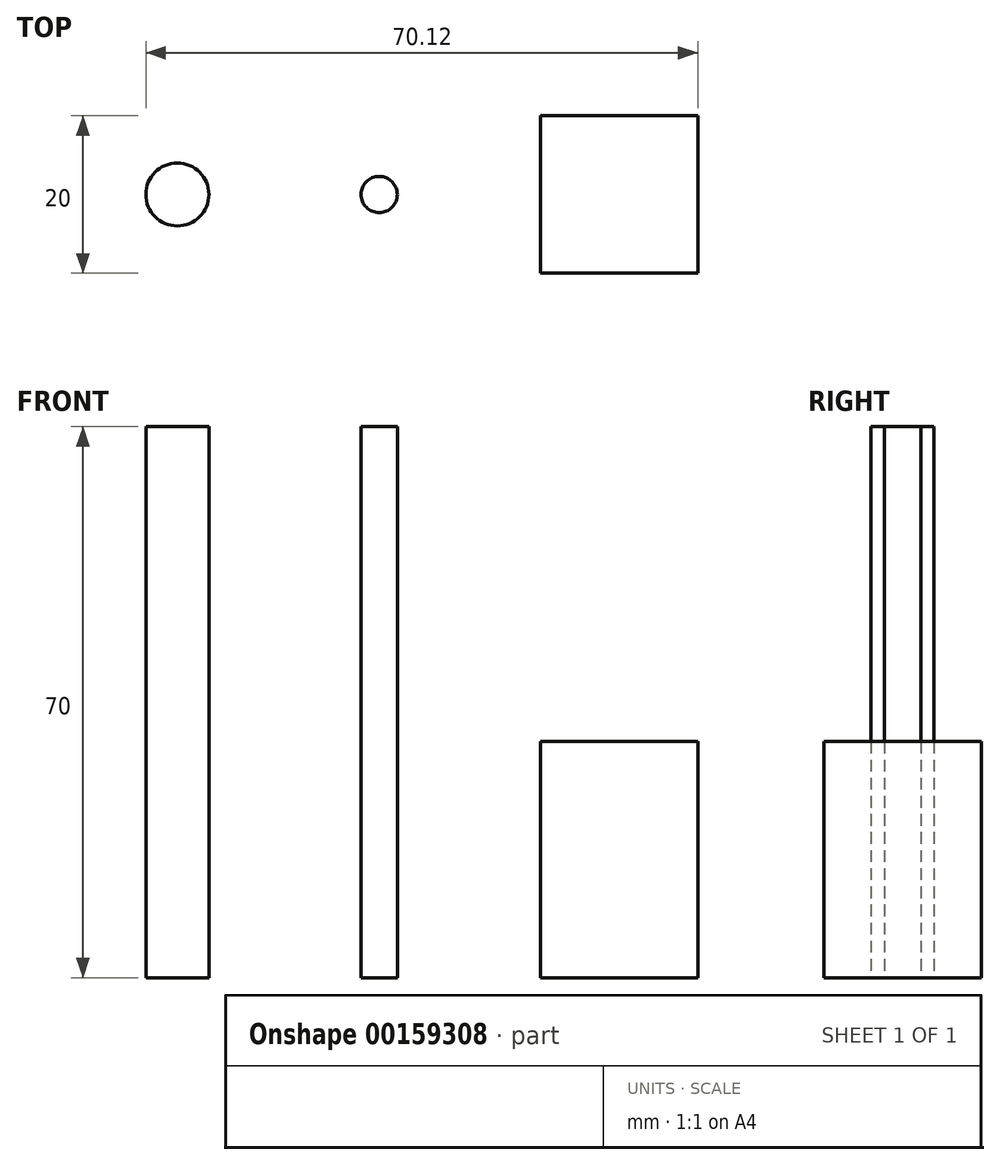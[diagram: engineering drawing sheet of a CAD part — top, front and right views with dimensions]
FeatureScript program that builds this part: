
annotation { "Feature Type Name" : "Feature", "Feature Type Description" : "" }
export const myFeature = defineFeature(function(context is Context, id is Id, definition is map)
    precondition{}
    {
        {
            var Q0;
            Q0=qCreatedBy(makeId("Top.planeOp"),FACE);
            var sketch = newSketch(context, id + "F0", { "sketchPlane" : qUnion([Q0])});
            skCircle(sketch, "E0", {"center": v(-16.16, 0) * mm, "radius": 4 * mm});
            skSolve(sketch);
        }
        {
            var Q0;
            Q0=makeQuery(id+"F0.imprint","IMPRINT",FACE,{"disambiguationData":[TD([[makeQuery(id+"F0.imprint","IMPRINT",EDGE,{"derivedFrom":sQuery(id+"F0.wireOp",EDGE,"E0")}),1.0]])]});
            extrude(context, id + "F1", {"entities" : qUnion([Q0]), "depth" : 70 * mm});
        }
        {
            var Q0;
            Q0=qCreatedBy(makeId("Top.planeOp"),FACE);
            var sketch = newSketch(context, id + "F2", { "sketchPlane" : qUnion([Q0])});
            skCircle(sketch, "E1", {"center": v(9.48, 0) * mm, "radius": 2.3 * mm});
            skSolve(sketch);
        }
        {
            var Q0;
            Q0 = qSketchRegion(id + "F2", true);
            extrude(context, id + "F3", {"entities" : qUnion([Q0]), "depth" : 70 * mm});
        }
        {
            var Q0;
            Q0=qCreatedBy(makeId("Top.planeOp"),FACE);
            var sketch = newSketch(context, id + "F4", { "sketchPlane" : qUnion([Q0])});
            skLineSegment(sketch, "E2.bottom", {"start": v(49.96, -10) * mm, "end": v(29.96, -10) * mm});
            skLineSegment(sketch, "E2.top", {"start": v(49.96, 10) * mm, "end": v(29.96, 10) * mm});
            skLineSegment(sketch, "E2.left", {"start": v(49.96, -10) * mm, "end": v(49.96, 10) * mm});
            skLineSegment(sketch, "E2.right", {"start": v(29.96, -10) * mm, "end": v(29.96, 10) * mm});
            skPoint(sketch, "E2.middle", {"position": v(39.96, 0) * mm});
            skSolve(sketch);
        }
        {
            var Q0;
            Q0 = qSketchRegion(id + "F4", true);
            extrude(context, id + "F5", {"entities" : qUnion([Q0]), "depth" : 30 * mm});
        }
    });
